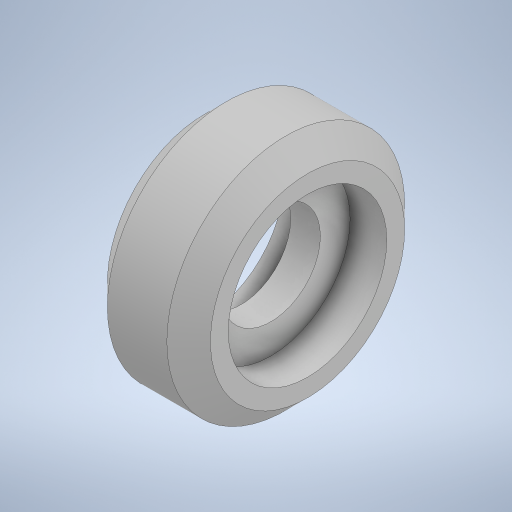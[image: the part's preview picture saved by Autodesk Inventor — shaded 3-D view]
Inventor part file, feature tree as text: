
AUTODESK INVENTOR PART (.ipt)
format: ipt  version: 2024.2 (Build 282272000, 272)  size: 253,440 bytes
history: native  units: in
note: dims shown in document units (in); Inventor stores cm internally (conversion verified against a paired STEP export)
features: extrude x1, sketch x1, other x1
ambient origin geometry x8: Origin, YZ Plane, XZ Plane, XY Plane, X Axis, Y Axis, Z Axis, Center Point
bodies: Solid1 (feature_tree)
feature tree (3):
  extrude  "Extrusion1"  Depth=0.3937in TaperAngle=0.0deg
  sketch  "Sketch1"  dims[d0=0.3937in d1=0.3937in d2=0.0in]
  other  "Corpo1"
